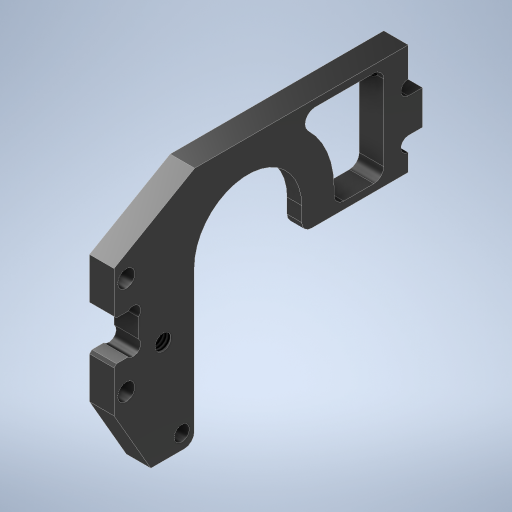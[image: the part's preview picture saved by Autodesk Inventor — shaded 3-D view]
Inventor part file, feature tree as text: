
AUTODESK INVENTOR PART (.ipt)
format: ipt  version: 2024.2 (Build 282272000, 272)  size: 543,744 bytes
history: native  units: mm
features: hole x3, extrude x2, sketch x2, other x1, chamfer x1
ambient origin geometry x8: Origin, YZ Plane, XZ Plane, XY Plane, X Axis, Y Axis, Z Axis, Center Point
bodies: Solid1 (feature_tree)
feature tree (9):
  other  "LegBaseSideFrameBasis.ipt"
  extrude  "Extrusion1"  Depth=5.0mm TaperAngle=0.0deg
  extrude  "Extrusion3"  Depth=2.0mm TaperAngle=45.0deg
  hole  "Phi3.5"  [1 undecoded]
  hole  "Phi3.1"  [1 undecoded]
  hole  "Side-M3"  [1 undecoded]
  chamfer  "C0.5"  [1 undecoded]
  sketch  "Sketch1"  dims[d0=10.0mm d1=5.0mm d2=0.0mm]
  sketch  "Sketch2"  dims[d5=2.0mm d6=0.0mm d7=3.5mm d8=6.0mm d9=4.0mm d10=2.0mm d11=90.0deg d12=8.0mm d13=20.594885mm d14=3.1mm d15=6.0mm d16=4.0mm d17=2.0mm d18=90.0deg d19=8.0mm d20=20.594885mm d21=0.5mm d22=2.0mm d23=45.0deg d27=2.0mm d29=3.242mm d30=8.0mm d31=4.0mm d32=2.0mm d33=90.0deg d34=8.0mm d35=0.0mm d36=9.5mm d37=2.0mm d38=60.0deg d39=2.459mm d40=6.0mm d41=4.0mm d42=2.0mm d43=90.0deg d44=6.0mm d45=0.0mm d28=1.0mm]
note: 4 required parameter values undecoded (feature->parameter linkage not recoverable at this tier; creation-order binding heuristic only, values carry confidence <= 0.55)
